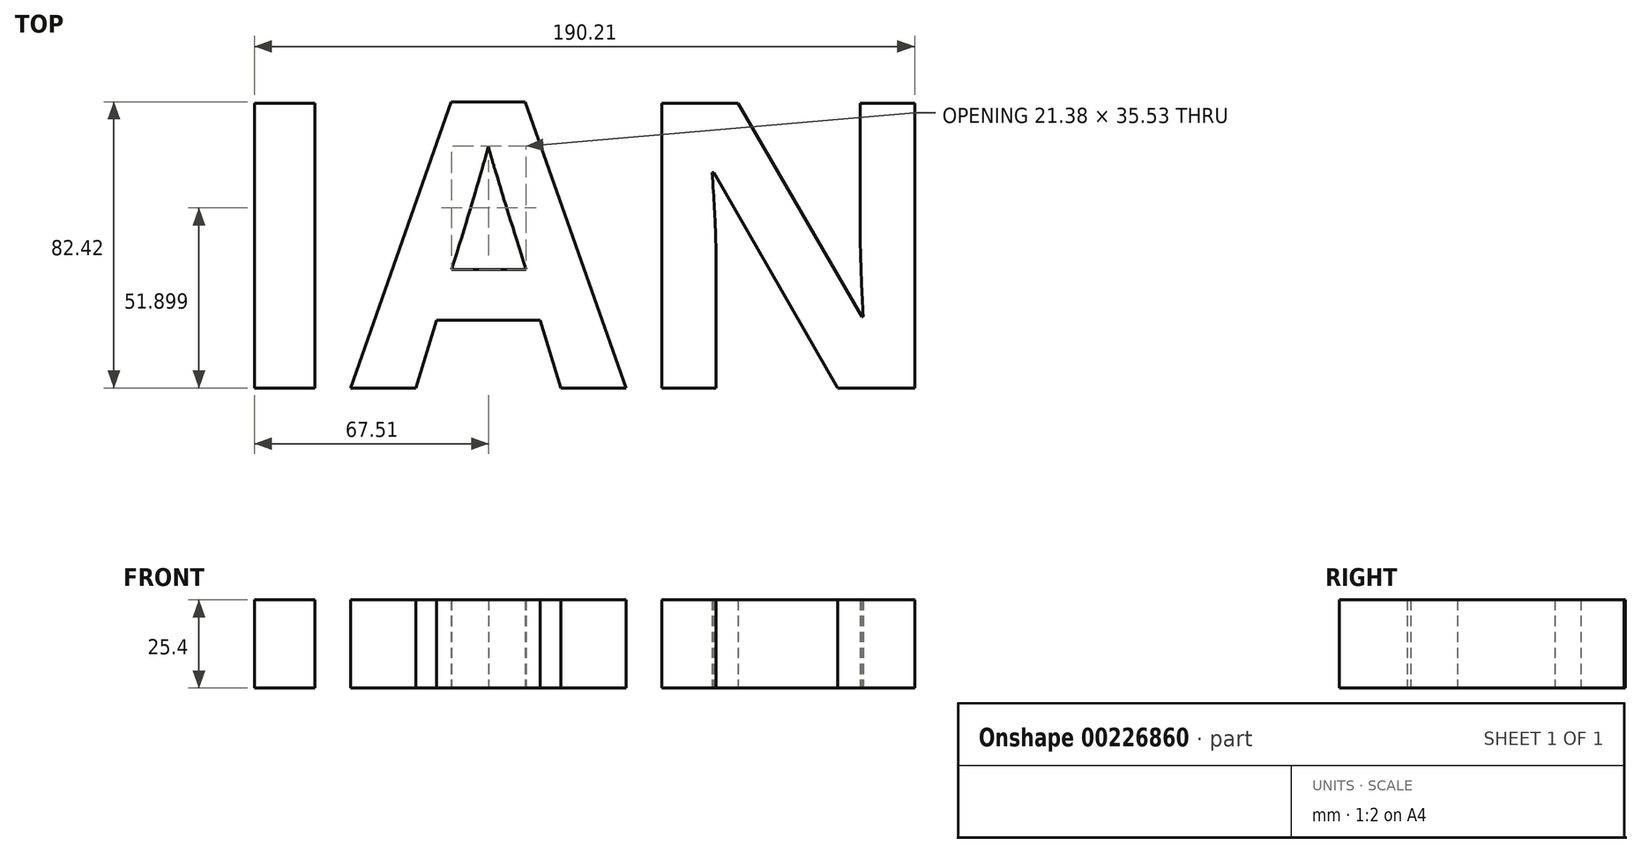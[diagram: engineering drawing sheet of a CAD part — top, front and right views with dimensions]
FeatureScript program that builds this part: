
annotation { "Feature Type Name" : "Feature", "Feature Type Description" : "" }
export const myFeature = defineFeature(function(context is Context, id is Id, definition is map)
    precondition{}
    {
        {
            var Q0;
            Q0=qCreatedBy(makeId("Top.planeOp"),FACE);
            var sketch = newSketch(context, id + "F0", { "sketchPlane" : qUnion([Q0])});
            skText(sketch, "E0", { "text": "IAN", "fontName": "OpenSans-Bold.ttf"});
            const initialGuessF0  = {"E0": [-0.10318, -0.04707, 1, 0, 0.08278]};
            skSetInitialGuess(sketch, initialGuessF0);
            skSolve(sketch);
        }
        {
            var Q0;
            Q0=makeQuery(id+"F0.imprint","IMPRINT",FACE,{"disambiguationData":[TD([[makeQuery(id+"F0.imprint","IMPRINT",EDGE,{"derivedFrom":sQuery(id+"F0.wireOp",EDGE,"E0.sketch_text.stroke-0")}),-1.0]])]});
            var Q1;
            Q1=makeQuery(id+"F0.imprint","IMPRINT",FACE,{"disambiguationData":[TD([[makeQuery(id+"F0.imprint","IMPRINT",EDGE,{"derivedFrom":sQuery(id+"F0.wireOp",EDGE,"E0.sketch_text.stroke-4")}),-1.0]])]});
            var Q2;
            Q2=makeQuery(id+"F0.imprint","IMPRINT",FACE,{"disambiguationData":[TD([[makeQuery(id+"F0.imprint","IMPRINT",EDGE,{"derivedFrom":sQuery(id+"F0.wireOp",EDGE,"E0.sketch_text.stroke-16")}),-1.0]])]});
            extrude(context, id + "F1", {"entities" : qUnion([Q0, Q1, Q2]), "depth" : 25.4 * mm});
        }
    });
